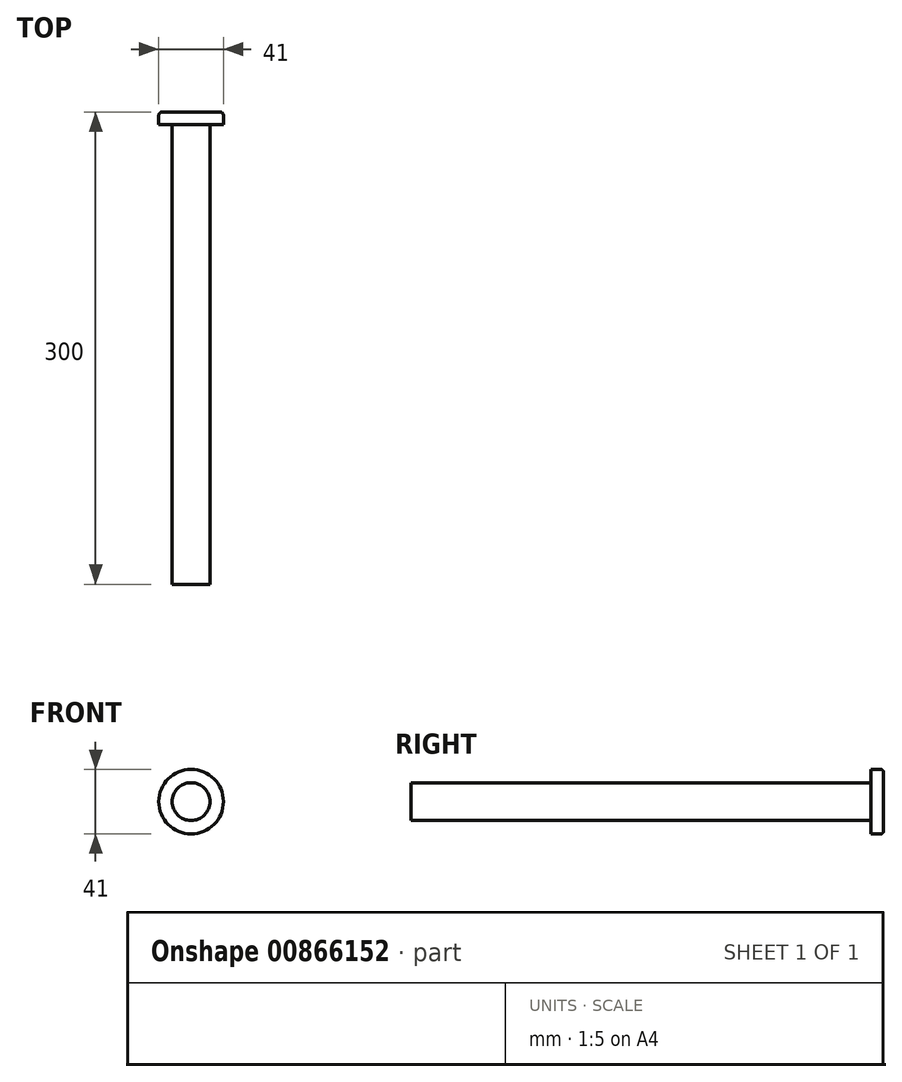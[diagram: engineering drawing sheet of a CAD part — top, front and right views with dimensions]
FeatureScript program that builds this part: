
annotation { "Feature Type Name" : "Feature", "Feature Type Description" : "" }
export const myFeature = defineFeature(function(context is Context, id is Id, definition is map)
    precondition{}
    {
        {
            var Q0;
            Q0=qCreatedBy(makeId("Front.planeOp"),FACE);
            var sketch = newSketch(context, id + "F0", { "sketchPlane" : qUnion([Q0])});
            skCircle(sketch, "E0", {"center": v(0, 0) * mm, "radius": 12 * mm});
            skCircle(sketch, "E1", {"center": v(0, 0) * mm, "radius": 20.5 * mm});
            skSolve(sketch);
        }
        {
            var Q0;
            Q0 = qSketchRegion(id + "F0", true);
            var Q1;
            Q1=makeQuery(id+"F0.imprint","IMPRINT",FACE,{"disambiguationData":[TD([[makeQuery(id+"F0.imprint","IMPRINT",EDGE,{"derivedFrom":sQuery(id+"F0.wireOp",EDGE,"E0")}),1.0]])]});
            extrude(context, id + "F1", {"entities" : qUnion([Q0, Q1]), "depth" : 8 * mm, "offsetDistance" : 25 * mm});
        }
        {
            var Q0;
            Q0=makeQuery(id+"F0.imprint","IMPRINT",FACE,{"disambiguationData":[TD([[makeQuery(id+"F0.imprint","IMPRINT",EDGE,{"derivedFrom":sQuery(id+"F0.wireOp",EDGE,"E0")}),1.0]])]});
            extrude(context, id + "F2", {"entities" : qUnion([Q0]), "operationType" : NewBodyOperationType.ADD, "depth" : 300 * mm, "offsetDistance" : 25 * mm});
        }
        {
            var Q0;
            Q0=makeQuery(id+"F1.opExtrude","CAP_EDGE",EDGE,{"disambiguationData":[OSD([sQuery(id+"F0.wireOp",EDGE,"E1")])],"isStart":true});
            fillet(context, id + "F3", {"entities" : qUnion([Q0]), "radius" : 2 * mm, "tangentPropagation" : true, "allowEdgeOverflow" : false});
        }
    });
